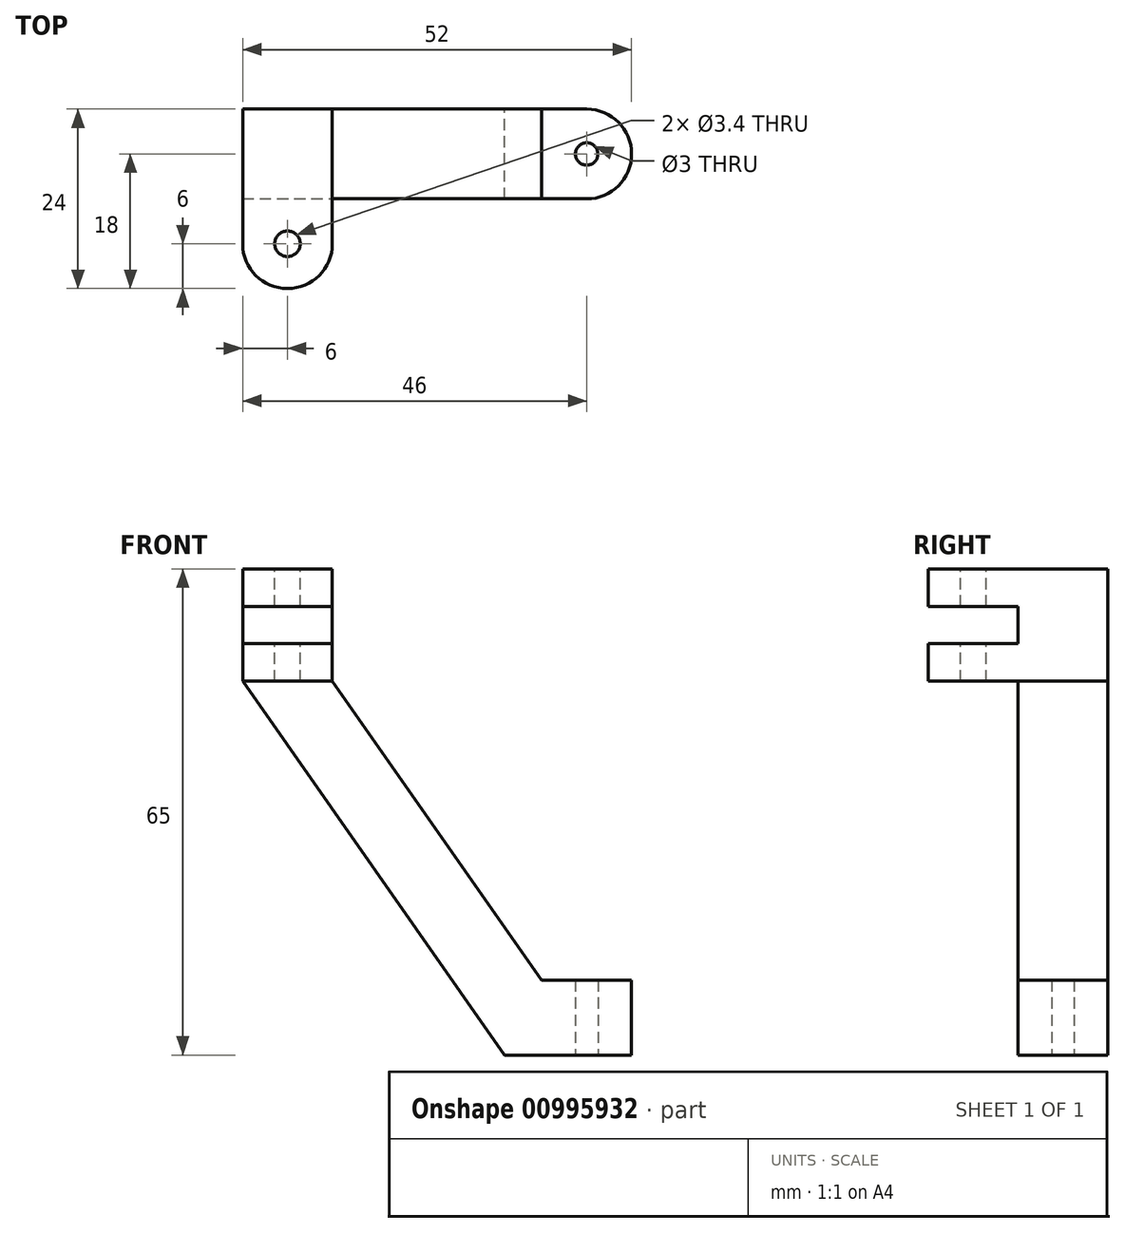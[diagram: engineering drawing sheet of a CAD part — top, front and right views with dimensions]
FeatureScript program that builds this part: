
annotation { "Feature Type Name" : "Feature", "Feature Type Description" : "" }
export const myFeature = defineFeature(function(context is Context, id is Id, definition is map)
    precondition{}
    {
        {
            var Q0;
            Q0=qCreatedBy(makeId("Top.planeOp"),FACE);
            var sketch = newSketch(context, id + "F0", { "sketchPlane" : qUnion([Q0])});
            skLineSegment(sketch, "E0.0", {"start": v(10, 10) * mm, "end": v(-30, 10) * mm});
            skLineSegment(sketch, "E0.2", {"start": v(-30, -2) * mm, "end": v(10, -2) * mm});
            skLineSegment(sketch, "E1", {"start": v(10, 10) * mm, "end": v(16, 10) * mm});
            skLineSegment(sketch, "E2", {"start": v(16, 10) * mm, "end": v(16, -2) * mm});
            skLineSegment(sketch, "E3", {"start": v(10, -2) * mm, "end": v(16, -2) * mm});
            skArc(sketch, "E4", {"start": v(16, -2) * mm, "mid": v(22, 4) * mm, "end": v(16, 10) * mm});
            skCircle(sketch, "E5", {"center": v(16, 4) * mm, "radius": 1.5 * mm});
            skArc(sketch, "E6", {"start": v(16, 10) * mm, "mid": v(10, 4) * mm, "end": v(16, -2) * mm});
            skLineSegment(sketch, "E7", {"start": v(10, -2) * mm, "end": v(10, 10) * mm});
            skLineSegment(sketch, "E8", {"start": v(-30, 10) * mm, "end": v(-30, -2) * mm});
            skSolve(sketch);
        }
        {
            var Q0;
            Q0=makeQuery(id+"F0.imprint","IMPRINT",FACE,{"disambiguationData":[TD([[makeQuery(id+"F0.imprint","IMPRINT",EDGE,{"derivedFrom":sQuery(id+"F0.wireOp",EDGE,"kl4RLzvs-neOC-4kaa-MvuH-81o4wounMt7W")}),-1.0]])]});
            var Q1;
            Q1=makeQuery(id+"F0.imprint","IMPRINT",FACE,{"disambiguationData":[TD([[makeQuery(id+"F0.imprint","IMPRINT",EDGE,{"derivedFrom":sQuery(id+"F0.wireOp",EDGE,"E0.1")}),-1.0]])]});
            var Q2;
            {var subQ1=sQuery(id+"F0.wireOp",EDGE,"E4");Q2=makeQuery(id+"F0.imprint","IMPRINT",FACE,{"disambiguationData":[TD([[makeQuery(id+"F0.imprint","IMPRINT",EDGE,{"derivedFrom":subQ1}),1.0]])]});}
            var Q3;
            {var subQ2=sQuery(id+"F0.wireOp",EDGE,"E2");var subQ6=sQuery(id+"F0.wireOp",EDGE,"E5");var subQ8=makeQuery(id+"F0.imprint","INTERSECT",VERTEX,{"disambiguationData":[OD(0.0)],"derivedFrom":[subQ2,subQ6]});Q3=makeQuery(id+"F0.imprint","IMPRINT",FACE,{"disambiguationData":[TD([[makeQuery(id+"F0.imprint","IMPRINT",EDGE,{"disambiguationData":[TD([[subQ8,-1.0]])],"derivedFrom":subQ6}),-1.0]])]});}
            var Q4;
            {var subQ0=sQuery(id+"F0.wireOp",EDGE,"55ea673d-e93c-4888-aa08-729aeeb4521a.trimOffspring");Q4=makeQuery(id+"F0.imprint","IMPRINT",FACE,{"disambiguationData":[TD([[makeQuery(id+"F0.imprint","IMPRINT",EDGE,{"derivedFrom":subQ0}),-1.0]])]});}
            var Q5;
            {var subQ4=sQuery(id+"F0.wireOp",EDGE,"E6");Q5=makeQuery(id+"F0.imprint","IMPRINT",FACE,{"disambiguationData":[TD([[makeQuery(id+"F0.imprint","IMPRINT",EDGE,{"derivedFrom":subQ4}),-1.0]])]});}
            extrude(context, id + "F1", {"entities" : qUnion([Q0, Q1, Q2, Q3, Q4, Q5]), "depth" : 20 * mm, "offsetDistance" : 25 * mm});
        }
        {
            var Q0;
            {var subQ1=sQuery(id+"F0.wireOp",EDGE,"E4");Q0=makeQuery(id+"F0.imprint","IMPRINT",FACE,{"disambiguationData":[TD([[makeQuery(id+"F0.imprint","IMPRINT",EDGE,{"derivedFrom":subQ1}),1.0]])]});}
            var Q1;
            {var subQ2=sQuery(id+"F0.wireOp",EDGE,"E2");var subQ6=sQuery(id+"F0.wireOp",EDGE,"E5");var subQ8=makeQuery(id+"F0.imprint","INTERSECT",VERTEX,{"disambiguationData":[OD(0.0)],"derivedFrom":[subQ2,subQ6]});Q1=makeQuery(id+"F0.imprint","IMPRINT",FACE,{"disambiguationData":[TD([[makeQuery(id+"F0.imprint","IMPRINT",EDGE,{"disambiguationData":[TD([[subQ8,-1.0]])],"derivedFrom":subQ6}),-1.0]])]});}
            var Q2;
            Q2=makeQuery(id+"F1.opExtrude","CAP_FACE",FACE,{"disambiguationData":[OSD([sQuery(id+"F0.wireOp",EDGE,"kl4RLzvs-neOC-4kaa-MvuH-81o4wounMt7W"),sQuery(id+"F0.wireOp",EDGE,"zpW9tX9X-YbCG-toYK-Ce4f-b6q3oF1lmya7"),sQuery(id+"F0.wireOp",EDGE,"UU2mt6Xs-SYPF-TyW4-shn7-l1qw8sopiLif"),sQuery(id+"F0.wireOp",EDGE,"E0.0"),sQuery(id+"F0.wireOp",EDGE,"E0.2"),sQuery(id+"F0.wireOp",EDGE,"E1"),sQuery(id+"F0.wireOp",EDGE,"E3"),sQuery(id+"F0.wireOp",EDGE,"E4"),sQuery(id+"F0.wireOp",EDGE,"E5"),sQuery(id+"F0.wireOp",EDGE,"zGBpB5mb-lHt2-OTn9-9MS7-HxHiJCcUgA3a"),sQuery(id+"F0.wireOp",EDGE,"LeM1kL8k-WXYL-SqW6-aEB5-R12wID98HVLa")])],"isStart":false});
            var Q3;
            {var subQ0=sQuery(id+"F0.wireOp",EDGE,"E3");Q3=makeQuery(id+"F0.imprint","IMPRINT",FACE,{"disambiguationData":[TD([[makeQuery(id+"F0.imprint","IMPRINT",EDGE,{"derivedFrom":subQ0}),1.0]])]});}
            var Q4;
            {var subQ0=sQuery(id+"F0.wireOp",EDGE,"E1");Q4=makeQuery(id+"F0.imprint","IMPRINT",FACE,{"disambiguationData":[TD([[makeQuery(id+"F0.imprint","IMPRINT",EDGE,{"derivedFrom":subQ0}),-1.0]])]});}
            extrude(context, id + "F2", {"entities" : qUnion([Q0, Q1, Q2, Q3, Q4]), "operationType" : NewBodyOperationType.REMOVE, "depth" : 20 * mm, "offsetDistance" : 25 * mm, "hasSecondDirection" : true, "secondDirectionOppositeDirection" : false, "secondDirectionDepth" : 10 * mm});
        }
        {
            var Q0;
            {var subQ1=sQuery(id+"F0.wireOp",EDGE,"E0.0");Q0=makeQuery(id+"F0.imprint","IMPRINT",FACE,{"disambiguationData":[TD([[makeQuery(id+"F0.imprint","IMPRINT",EDGE,{"derivedFrom":subQ1}),1.0]])]});}
            extrude(context, id + "F3", {"entities" : qUnion([Q0]), "operationType" : NewBodyOperationType.ADD, "depth" : 50 * mm, "offsetDistance" : 25 * mm});
        }
        {
            var Q0;
            Q0=makeQuery(id+"F3.boolean.opBoolean","MERGE",FACE,{"derivedFrom":[makeQuery(id+"F1.opExtrude","SWEPT_FACE",FACE,{"disambiguationData":[OSD([sQuery(id+"F0.wireOp",EDGE,"E1")])]}),makeQuery(id+"F3.opExtrude","SWEPT_FACE",FACE,{"disambiguationData":[OSD([sQuery(id+"F0.wireOp",EDGE,"E0.0")])]})]});
            var sketch = newSketch(context, id + "F4", { "sketchPlane" : qUnion([Q0])});
            skLineSegment(sketch, "E9", {"start": v(-10, 10) * mm, "end": v(18, 50) * mm});
            skLineSegment(sketch, "E10", {"start": v(18, 50) * mm, "end": v(30, 50) * mm});
            skLineSegment(sketch, "E11", {"start": v(30, 50) * mm, "end": v(-5, 0) * mm});
            skLineSegment(sketch, "E12", {"start": v(-5, 0) * mm, "end": v(-16, 0) * mm});
            skLineSegment(sketch, "E13", {"start": v(-16, 0) * mm, "end": v(-16, 10) * mm});
            skLineSegment(sketch, "E14", {"start": v(-16, 10) * mm, "end": v(-10, 10) * mm});
            skSolve(sketch);
        }
        {
            var Q0;
            {var subQ0=sQuery(id+"F4.wireOp",EDGE,"E9");Q0=makeQuery(id+"F4.imprint","IMPRINT",FACE,{"disambiguationData":[TD([[makeQuery(id+"F4.imprint","IMPRINT",EDGE,{"derivedFrom":subQ0}),1.0]])]});}
            var Q1;
            {var subQ0=sQuery(id+"F4.wireOp",EDGE,"E11");Q1=makeQuery(id+"F4.imprint","IMPRINT",FACE,{"disambiguationData":[TD([[makeQuery(id+"F4.imprint","IMPRINT",EDGE,{"derivedFrom":subQ0}),1.0]])]});}
            extrude(context, id + "F5", {"entities" : qUnion([Q0, Q1]), "operationType" : NewBodyOperationType.REMOVE, "endBound" : BoundingType.THROUGH_ALL, "oppositeDirection" : true, "depth" : 25 * mm, "offsetDistance" : 25 * mm});
        }
        {
            var Q0;
            Q0=makeQuery(id+"F3.opExtrude","CAP_FACE",FACE,{"disambiguationData":[OSD([sQuery(id+"F0.wireOp",EDGE,"E0.0"),sQuery(id+"F0.wireOp",EDGE,"E0.2"),sQuery(id+"F0.wireOp",EDGE,"E7"),sQuery(id+"F0.wireOp",EDGE,"E8")])],"isStart":false});
            extrude(context, id + "F6", {"entities" : qUnion([Q0]), "operationType" : NewBodyOperationType.ADD, "depth" : 15 * mm, "offsetDistance" : 25 * mm});
        }
        {
            var Q0;
            {var subQ0=sQuery(id+"F0.wireOp",EDGE,"E0.2");Q0=makeQuery(id+"F6.boolean.opBoolean","MERGE",FACE,{"derivedFrom":[makeQuery(id+"F3.boolean.opBoolean","MERGE",FACE,{"derivedFrom":[makeQuery(id+"F1.opExtrude","SWEPT_FACE",FACE,{"disambiguationData":[OSD([sQuery(id+"F0.wireOp",EDGE,"E3")])]}),makeQuery(id+"F3.opExtrude","SWEPT_FACE",FACE,{"disambiguationData":[OSD([subQ0])]})]}),makeQuery(id+"F6.opExtrude","SWEPT_FACE",FACE,{"disambiguationData":[OSD([subQ0])]})]});}
            var sketch = newSketch(context, id + "F7", { "sketchPlane" : qUnion([Q0])});
            skLineSegment(sketch, "E15", {"start": v(-30, 50) * mm, "end": v(-18, 50) * mm});
            skLineSegment(sketch, "E16", {"start": v(-18, 50) * mm, "end": v(-18, 65) * mm});
            skLineSegment(sketch, "E17", {"start": v(-18, 65) * mm, "end": v(-30, 65) * mm});
            skLineSegment(sketch, "E18", {"start": v(-30, 65) * mm, "end": v(-30, 50) * mm});
            skLineSegment(sketch, "E19", {"start": v(-30, 55) * mm, "end": v(-18, 55) * mm});
            skLineSegment(sketch, "E20", {"start": v(-30, 60) * mm, "end": v(-18, 60) * mm});
            skLineSegment(sketch, "E21", {"start": v(-30, 57.5) * mm, "end": v(-18, 57.5) * mm, "construction": true});
            skSolve(sketch);
        }
        {
            var Q0;
            {var subQ0=sQuery(id+"F7.wireOp",EDGE,"E15");Q0=makeQuery(id+"F7.imprint","IMPRINT",FACE,{"disambiguationData":[TD([[makeQuery(id+"F7.imprint","IMPRINT",EDGE,{"derivedFrom":subQ0}),1.0]])]});}
            var Q1;
            {var subQ0=sQuery(id+"F7.wireOp",EDGE,"E17");Q1=makeQuery(id+"F7.imprint","IMPRINT",FACE,{"disambiguationData":[TD([[makeQuery(id+"F7.imprint","IMPRINT",EDGE,{"derivedFrom":subQ0}),-1.0]])]});}
            extrude(context, id + "F8", {"entities" : qUnion([Q0, Q1]), "operationType" : NewBodyOperationType.ADD, "depth" : 12 * mm, "offsetDistance" : 25 * mm});
        }
        {
            var Q0;
            {var subQ0=sQuery(id+"F7.wireOp",EDGE,"E18");Q0=makeQuery(id+"F8.opExtrude","CAP_EDGE",EDGE,{"disambiguationData":[OSD([subQ0]),TDD([makeQuery(id+"F7.imprint","IMPRINT",EDGE,{"disambiguationData":[TD([[makeQuery(id+"F7.imprint","INTERSECT",VERTEX,{"derivedFrom":[sQuery(id+"F7.wireOp",EDGE,"E17"),subQ0]}),-1.0]])],"derivedFrom":subQ0})])],"isStart":false});}
            var Q1;
            {var subQ0=sQuery(id+"F7.wireOp",EDGE,"E16");Q1=makeQuery(id+"F8.opExtrude","CAP_EDGE",EDGE,{"disambiguationData":[OSD([subQ0]),TDD([makeQuery(id+"F7.imprint","IMPRINT",EDGE,{"disambiguationData":[TD([[makeQuery(id+"F7.imprint","INTERSECT",VERTEX,{"derivedFrom":[subQ0,sQuery(id+"F7.wireOp",EDGE,"E17")]}),-1.0]])],"derivedFrom":subQ0})])],"isStart":false});}
            var Q2;
            {var subQ0=sQuery(id+"F7.wireOp",EDGE,"E16");Q2=makeQuery(id+"F8.opExtrude","CAP_EDGE",EDGE,{"disambiguationData":[OSD([subQ0]),TDD([makeQuery(id+"F7.imprint","IMPRINT",EDGE,{"disambiguationData":[TD([[makeQuery(id+"F7.imprint","INTERSECT",VERTEX,{"derivedFrom":[subQ0,sQuery(id+"F7.wireOp",EDGE,"E19")]}),-1.0]])],"derivedFrom":subQ0})])],"isStart":false});}
            var Q3;
            {var subQ0=sQuery(id+"F7.wireOp",EDGE,"E18");Q3=makeQuery(id+"F8.opExtrude","CAP_EDGE",EDGE,{"disambiguationData":[OSD([subQ0]),TDD([makeQuery(id+"F7.imprint","IMPRINT",EDGE,{"disambiguationData":[TD([[makeQuery(id+"F7.imprint","INTERSECT",VERTEX,{"derivedFrom":[subQ0,sQuery(id+"F7.wireOp",EDGE,"E19")]}),-1.0]])],"derivedFrom":subQ0})])],"isStart":false});}
            fillet(context, id + "F9", {"entities" : qUnion([Q0, Q1, Q2, Q3]), "tangentPropagation" : true, "radius" : 6 * mm, "defaultsChanged" : true, "vertexSettings" : [], "allowEdgeOverflow" : false});
        }
        {
            var Q0;
            Q0=makeQuery(id+"F8.boolean.opBoolean","MERGE",FACE,{"derivedFrom":[makeQuery(id+"F6.opExtrude","CAP_FACE",FACE,{"disambiguationData":[OSD([sQuery(id+"F0.wireOp",EDGE,"E0.0"),sQuery(id+"F0.wireOp",EDGE,"E0.2"),sQuery(id+"F0.wireOp",EDGE,"E7"),sQuery(id+"F0.wireOp",EDGE,"E8")])],"isStart":false}),makeQuery(id+"F8.opExtrude","SWEPT_FACE",FACE,{"disambiguationData":[OSD([sQuery(id+"F7.wireOp",EDGE,"E17")])]})]});
            var sketch = newSketch(context, id + "F10", { "sketchPlane" : qUnion([Q0])});
            skLineSegment(sketch, "E22", {"start": v(-24, 10) * mm, "end": v(-24, -8) * mm});
            skSolve(sketch);
        }
        {
            var Q0;
            Q0=sQuery(id+"F10.wireOp",VERTEX,"E22.end");
            var Q1;
            Q1=makeQuery(id+"F1.opExtrude","SWEPT_BODY",BODY,{"disambiguationData":[OSD([sQuery(id+"F0.wireOp",EDGE,"E1"),sQuery(id+"F0.wireOp",EDGE,"E3"),sQuery(id+"F0.wireOp",EDGE,"E4"),sQuery(id+"F0.wireOp",EDGE,"E5"),sQuery(id+"F0.wireOp",EDGE,"E7")])]});
            hole(context, id + "F11", {"style" : HoleStyle.SIMPLE, "endStyle" : HoleEndStyle.THROUGH, "standardTappedOrClearance" : lookupTablePath({ "fit" : "Normal", "standard" : "ISO", "size" : "M3", "type" : "Clearance" }), "standardBlindInLast" : lookupTablePath({ "fit" : "Normal", "standard" : "ISO", "engagement" : "75%", "pitch" : "0.5 mm", "size" : "M3", "type" : "Clearance & tapped" }), "holeDiameter" : 3.4 * mm, "majorDiameter" : 5 * mm, "isTappedThrough" : true, "tappedDepth" : 12 * mm, "tapClearance" : 3, "locations" : qUnion([Q0]), "scope" : qUnion([Q1])});
        }
    });
